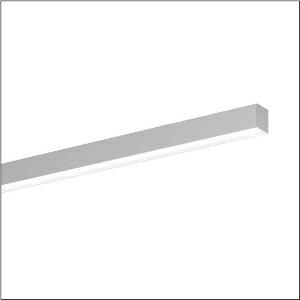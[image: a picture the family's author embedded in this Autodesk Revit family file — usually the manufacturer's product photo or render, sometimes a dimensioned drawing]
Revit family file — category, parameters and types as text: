
# Revit family: silica_21_51mx23tbt5s
name_source: partatom
category: Lighting Fixtures
units: mm (PartAtom-declared; Revit-internal decimal feet)

## family parameters
Cut with Voids When Loaded = No
Host = Face
Light Source = No
Part Type = Normal
Room Calculation Point = No
Round Connector Dimension = Use Diameter
Shared = No

## types (1)
- --- (1 x LED, 4030 lm, 40.5 W, 6500K)
    Apparent Load = 41 VA
    CIE Flux Codes = 78 96 99 100 100
    Color Rendering = 80
    Color Temperature = 6500K
    Default Elevation = 1800 mm
    Description = Silica 21, office luminaire, primary optical cover: prismatic diffuser, of PMMA, CAT 2 (L<= 3000cd/m²), light emission: direct distribution, primary light characteristic: symmetric, installation type: surface-mounted, LED, rated luminous flux: 4.030lm, luminous efficacy: 95lm/W, light colour: 8tw, colour temperature: 2700..6500K, control gear: DALI DT8, with terminal, 3+2-pole, max. 2.5mm², mains connection: 220..240V, AC, 50/60Hz, rated input power: 42.6W, luminaire housing, of aluminium, metallic grey (RAL 9006), length: 1.504mm, width: 53mm, height: 53mm, protection rating (complete): IP20, insulation class (complete): insulation class I (protective earthing), certification: CE, permissible operating ambient temperature: 0..+35°C, standard: EN 50419, packaging unit: 1 piece
    Height = 53 mm
    Lamp = 1 x LED
    Lamp Light Flux = 4030 lm
    Lamp Power = 40.5 W
    Lamp count = 1
    Length = 1504 mm
    Luminous efficacy = 100 lm/W
    Manufacturer = Siteco
    ModVariant = No
    Model = 51MX23TBT5S
    Mounting Place = Ceiling
    Mounting Type = Surface mounted
    Number of Poles = 1
    OnlyDefault = Yes
    Power Factor = 1
    Product Name = Silica 21
    Product group = office luminaire | ceiling mounted
    ProductGroupID = 301
    Protection Class = Protection class I
    Protection Degree = IP 20
    RLX_Detail_Level = 1
    RLX_Emergency_Light_Flux = 0 lm
    RLX_Emergency_Type = 0
    RLX_Emergency_Type_DB = No
    RlxData = <blob elided: 17973 chars, md5=c68a298e>
    Socket = socket
    Standby Power = 0 W
    System Light Flux = 4030 lm
    System Power = 41 W
    Type Comments = individual setting
    Type Image = l_1335933.jpg
    URL = http://relux.com
    VarID = @adj_140845
    Voltage = 0 V
    Weight = 0.00 kg
    Width = 53 mm

## geometry (parser evidence)
native form markers: Blend x4, Sweep x10
no freeform markers — native parametric forms only
